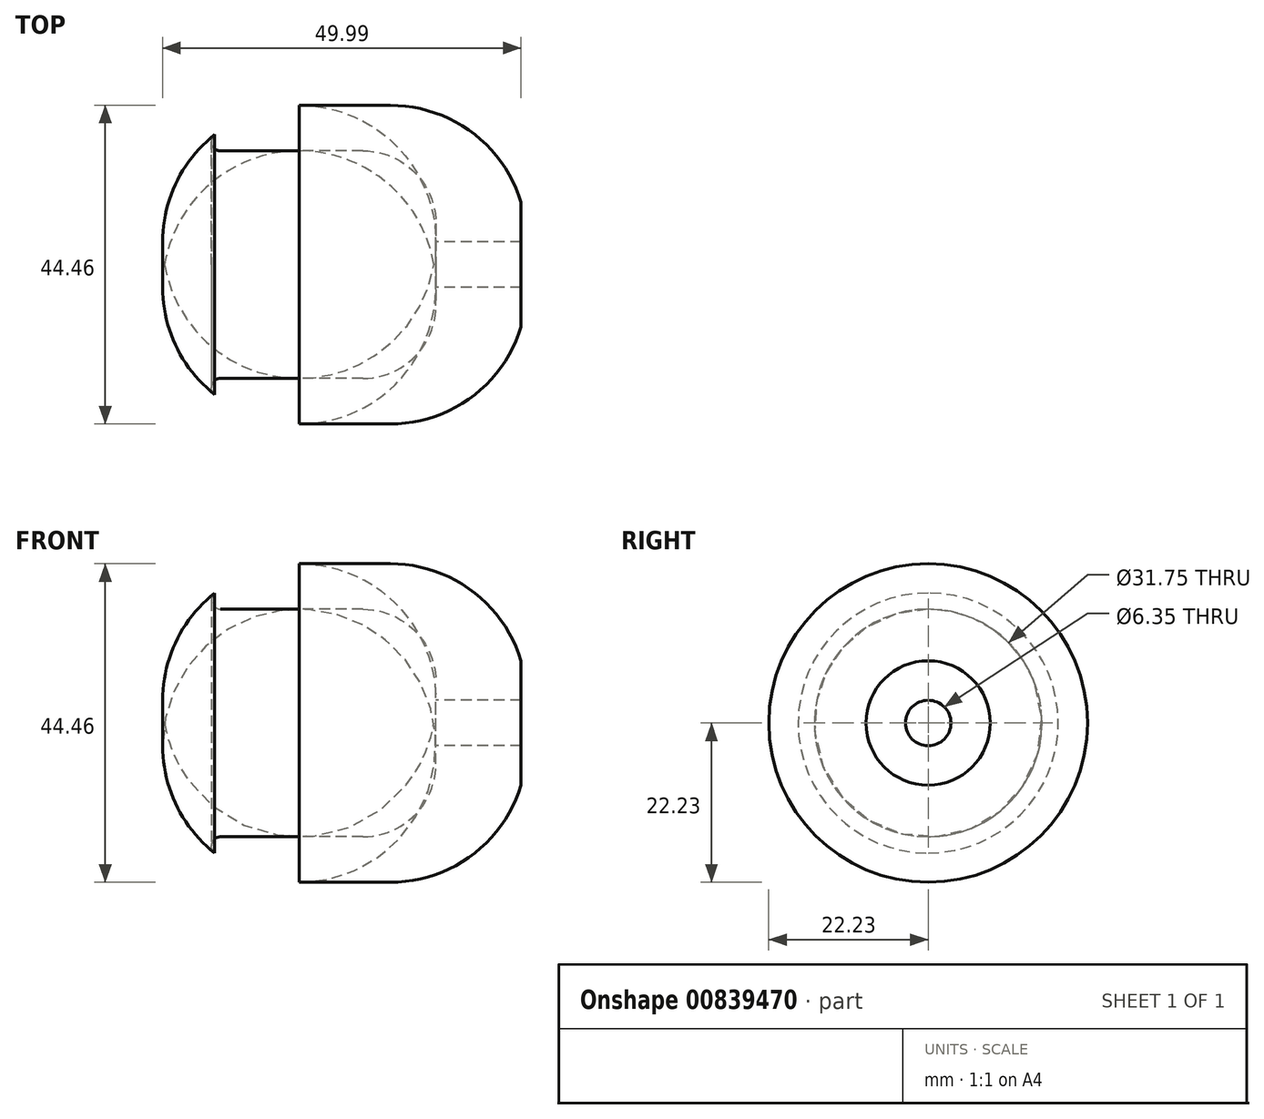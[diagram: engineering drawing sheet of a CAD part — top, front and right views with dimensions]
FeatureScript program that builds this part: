
annotation { "Feature Type Name" : "Feature", "Feature Type Description" : "" }
export const myFeature = defineFeature(function(context is Context, id is Id, definition is map)
    precondition{}
    {
        {
            var Q0;
            Q0=qCreatedBy(makeId("Right.planeOp"),FACE);
            var sketch = newSketch(context, id + "F0", { "sketchPlane" : qUnion([Q0])});
            skCircle(sketch, "E0", {"center": v(0, 0) * mm, "radius": 22.23 * mm});
            skSolve(sketch);
        }
        {
            var Q0;
            Q0=makeQuery(id+"F0.imprint","IMPRINT",FACE,{"disambiguationData":[TD([[makeQuery(id+"F0.imprint","IMPRINT",EDGE,{"derivedFrom":sQuery(id+"F0.wireOp",EDGE,"E0")}),1.0]])]});
            extrude(context, id + "F1", {"entities" : qUnion([Q0]), "depth" : 50.8 * mm, "offsetDistance" : 25.4 * mm});
        }
        {
            var Q0;
            Q0=makeQuery(id+"F1.opExtrude","CAP_EDGE",EDGE,{"disambiguationData":[OSD([sQuery(id+"F0.wireOp",EDGE,"E0")])],"isStart":true});
            var Q1;
            Q1=makeQuery(id+"F1.opExtrude","CAP_EDGE",EDGE,{"disambiguationData":[OSD([sQuery(id+"F0.wireOp",EDGE,"E0")])],"isStart":false});
            fillet(context, id + "F2", {"entities" : qUnion([Q0, Q1]), "radius" : 19.05 * mm, "tangentPropagation" : true, "allowEdgeOverflow" : false});
        }
        {
            var Q0;
            Q0=qCreatedBy(makeId("Right.planeOp"),FACE);
            var sketch = newSketch(context, id + "F3", { "sketchPlane" : qUnion([Q0])});
            skCircle(sketch, "E1", {"center": v(0, 0) * mm, "radius": 15.88 * mm});
            skSolve(sketch);
        }
        {
            var Q0;
            Q0 = qSketchRegion(id + "F3", true);
            extrude(context, id + "F4", {"entities" : qUnion([Q0]), "operationType" : NewBodyOperationType.REMOVE, "depth" : 38.1 * mm, "offsetDistance" : 25.4 * mm});
        }
        {
            var Q0;
            Q0=makeQuery(id+"F4.boolean.opBoolean","INTERSECT",EDGE,{"derivedFrom":[makeQuery(id+"F2.opFillet","BLEND_FACE",FACE,{"disambiguationData":[OSD([sQuery(id+"F0.wireOp",EDGE,"E0")])]}),makeQuery(id+"F4.opExtrude","SWEPT_FACE",FACE,{"disambiguationData":[OSD([sQuery(id+"F3.wireOp",EDGE,"E1")])]})]});
            fillet(context, id + "F5", {"entities" : qUnion([Q0]), "radius" : 1.27 * mm, "tangentPropagation" : true, "allowEdgeOverflow" : false});
        }
        {
            var Q0;
            Q0=qCreatedBy(makeId("Right.planeOp"),FACE);
            var sketch = newSketch(context, id + "F6", { "sketchPlane" : qUnion([Q0])});
            skCircle(sketch, "E2", {"center": v(0, 0) * mm, "radius": 3.18 * mm});
            skSolve(sketch);
        }
        {
            var Q0;
            Q0 = qSketchRegion(id + "F6", true);
            extrude(context, id + "F7", {"entities" : qUnion([Q0]), "operationType" : NewBodyOperationType.REMOVE, "endBound" : BoundingType.THROUGH_ALL, "depth" : 25.4 * mm, "offsetDistance" : 25.4 * mm});
        }
        {
            var Q0;
            Q0=makeQuery(id+"F4.boolean.opBoolean","COPY",EDGE,{"derivedFrom":makeQuery(id+"F4.opExtrude","CAP_EDGE",EDGE,{"disambiguationData":[OSD([sQuery(id+"F3.wireOp",EDGE,"E1")])],"isStart":false})});
            fillet(context, id + "F8", {"entities" : qUnion([Q0]), "radius" : 10.16 * mm, "tangentPropagation" : true, "allowEdgeOverflow" : false});
        }
        {
            var Q0;
            Q0=qCreatedBy(makeId("Front.planeOp"),FACE);
            var sketch = newSketch(context, id + "F9", { "sketchPlane" : qUnion([Q0])});
            skLineSegment(sketch, "E3.bottom", {"start": v(56.62, 8.82) * mm, "end": v(49.99, 8.82) * mm});
            skLineSegment(sketch, "E3.top", {"start": v(56.62, -11.12) * mm, "end": v(49.99, -11.12) * mm});
            skLineSegment(sketch, "E3.left", {"start": v(56.62, 8.82) * mm, "end": v(56.62, -11.12) * mm});
            skLineSegment(sketch, "E3.right", {"start": v(49.99, 8.82) * mm, "end": v(49.99, -11.12) * mm});
            skSolve(sketch);
        }
        {
            var Q0;
            Q0=makeQuery(id+"F9.imprint","IMPRINT",FACE,{"disambiguationData":[TD([[makeQuery(id+"F9.imprint","IMPRINT",EDGE,{"derivedFrom":sQuery(id+"F9.wireOp",EDGE,"E3.bottom")}),1.0]])]});
            extrude(context, id + "F10", {"entities" : qUnion([Q0]), "operationType" : NewBodyOperationType.REMOVE, "endBound" : BoundingType.THROUGH_ALL, "oppositeDirection" : true, "depth" : 25.4 * mm, "offsetDistance" : 25.4 * mm, "hasSecondDirection" : true, "secondDirectionOppositeDirection" : false, "secondDirectionDepth" : 25.4 * mm});
        }
    });
